# Revit family: ASL_Designline_Al_Door_Pillar_Small
name_source: partatom
category: Detail Items
revit_build: Autodesk Revit 2018 (Build: 20170223_1515(x64)
units: mm (PartAtom-declared; Revit-internal decimal feet)

## family parameters
Rotate with component = No
Section Shape = Not Defined
Shared = Yes

## types (3) — shared parameters
50mm Door Jamb Standard = Yes
Manufacturer = Aluminate Solutions Limited
Technical Info = www.aluminate.nz

## per-type parameters (varying)
| type | ASL Hinge Stile Hinge Door 100mm | ASL Hinge Stile Hinge Door 125mm | ASL Hinge Stile Hinge Door 75mm | Type Comments |
| Single Action ASL Hinge Stile Door Suite 125mm | No | Yes | No | ASL Designline Small Pillar With Single Action ASL 125mm Door Suite |
| Single Action ASL Hinge Stile Door Suite 100mm | Yes | No | No | ASL Designline Small Pillar With Single Action ASL 100mm Door Suite |
| Single Action ASL Hinge Stile Door Suite 75mm | No | No | Yes | ASL Designline Small Pillar With Single Action ASL 75mm Door Suite |

## geometry (parser evidence)
native form markers: Sweep x8
no freeform markers — native parametric forms only
